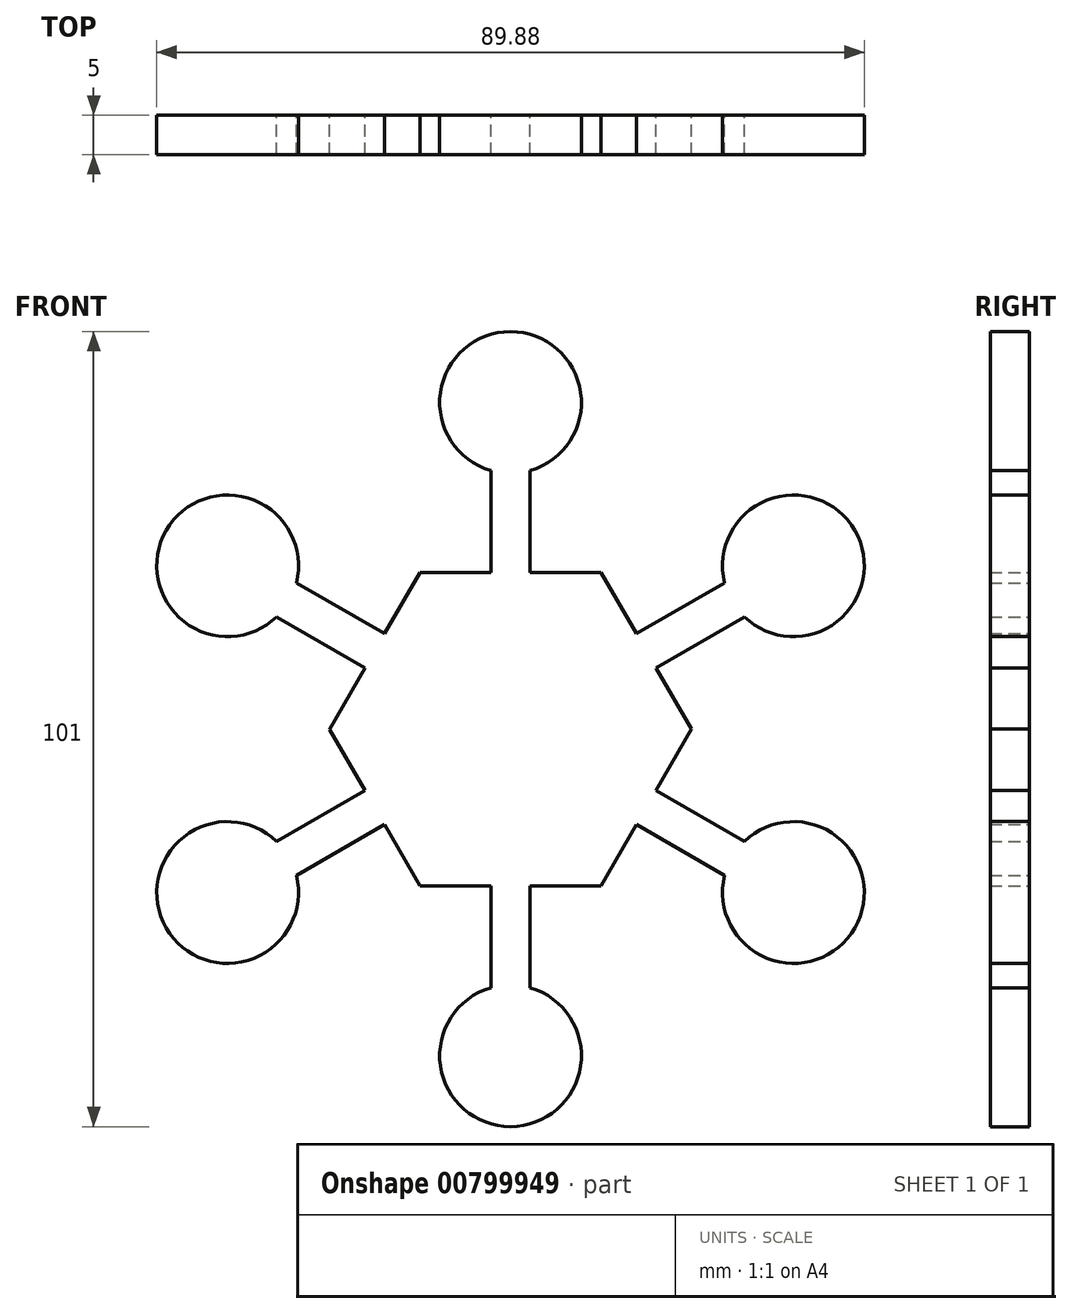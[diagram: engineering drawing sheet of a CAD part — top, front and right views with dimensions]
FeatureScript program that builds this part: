
annotation { "Feature Type Name" : "Feature", "Feature Type Description" : "" }
export const myFeature = defineFeature(function(context is Context, id is Id, definition is map)
    precondition{}
    {
        {
            var Q0;
            Q0=qCreatedBy(makeId("Front.planeOp"),FACE);
            var sketch = newSketch(context, id + "F0", { "sketchPlane" : qUnion([Q0])});
            skLineSegment(sketch, "E0.0", {"start": v(11.49, 19.92) * mm, "end": v(16, 12.12) * mm});
            skLineSegment(sketch, "E0.1", {"start": v(23, 0.01) * mm, "end": v(18.5, -7.8) * mm});
            skLineSegment(sketch, "E0.2", {"start": v(11.51, -19.91) * mm, "end": v(2.5, -19.92) * mm});
            skLineSegment(sketch, "E0.3", {"start": v(-11.49, -19.92) * mm, "end": v(-16, -12.12) * mm});
            skLineSegment(sketch, "E0.4", {"start": v(-23, -0.01) * mm, "end": v(-18.5, 7.8) * mm});
            skLineSegment(sketch, "E0.5", {"start": v(-11.51, 19.91) * mm, "end": v(-2.5, 19.92) * mm});
            skPoint(sketch, "E0.0.midPoint", {"position": v(17.24, 9.97) * mm});
            skLineSegment(sketch, "E1.top", {"start": v(-2.5, 0) * mm, "end": v(2.5, 0) * mm});
            skLineSegment(sketch, "E1.left", {"start": v(-2.5, 32.85) * mm, "end": v(-2.5, 19.76) * mm});
            skLineSegment(sketch, "E1.right", {"start": v(2.5, 32.85) * mm, "end": v(2.5, 19.76) * mm});
            skLineSegment(sketch, "E2.trimOffspring", {"start": v(2.5, 19.92) * mm, "end": v(11.49, 19.92) * mm});
            skArc(sketch, "E3.2.0", {"start": v(2.5, 32.85) * mm, "mid": v(0, 50.5) * mm, "end": v(-2.5, 32.85) * mm});
            skArc(sketch, "E4.1.0", {"start": v(-27.2, 18.6) * mm, "mid": v(-43.73, 25.25) * mm, "end": v(-29.7, 14.26) * mm});
            skArc(sketch, "E4.2.0", {"start": v(-29.7, -14.26) * mm, "mid": v(-43.73, -25.25) * mm, "end": v(-27.2, -18.6) * mm});
            skArc(sketch, "E4.3.0", {"start": v(-2.5, -32.85) * mm, "mid": v(0, -50.5) * mm, "end": v(2.5, -32.85) * mm});
            skArc(sketch, "E4.4.0", {"start": v(27.2, -18.6) * mm, "mid": v(43.73, -25.25) * mm, "end": v(29.7, -14.26) * mm});
            skArc(sketch, "E4.5.0", {"start": v(29.7, 14.26) * mm, "mid": v(43.73, 25.25) * mm, "end": v(27.2, 18.6) * mm});
            skPoint(sketch, "E4.center", {"position": v(0, 0) * mm});
            skLineSegment(sketch, "E5.1.0", {"start": v(-27.2, 18.6) * mm, "end": v(-15.86, 12.05) * mm});
            skLineSegment(sketch, "E5.1.1", {"start": v(-29.7, 14.26) * mm, "end": v(-18.36, 7.72) * mm});
            skLineSegment(sketch, "E5.2.0", {"start": v(-29.7, -14.26) * mm, "end": v(-18.36, -7.72) * mm});
            skLineSegment(sketch, "E5.2.1", {"start": v(-27.2, -18.6) * mm, "end": v(-15.86, -12.05) * mm});
            skLineSegment(sketch, "E5.3.0", {"start": v(-2.5, -32.85) * mm, "end": v(-2.5, -19.76) * mm});
            skLineSegment(sketch, "E5.3.1", {"start": v(2.5, -32.85) * mm, "end": v(2.5, -19.76) * mm});
            skLineSegment(sketch, "E5.4.0", {"start": v(27.2, -18.6) * mm, "end": v(15.86, -12.05) * mm});
            skLineSegment(sketch, "E5.4.1", {"start": v(29.7, -14.26) * mm, "end": v(18.36, -7.72) * mm});
            skLineSegment(sketch, "E5.5.0", {"start": v(29.7, 14.26) * mm, "end": v(18.36, 7.72) * mm});
            skLineSegment(sketch, "E5.5.1", {"start": v(27.2, 18.6) * mm, "end": v(15.86, 12.05) * mm});
            skLineSegment(sketch, "E6.trimOffspring", {"start": v(-16, 12.13) * mm, "end": v(-11.51, 19.91) * mm});
            skLineSegment(sketch, "E7.trimOffspring", {"start": v(-18.5, -7.8) * mm, "end": v(-23, -0.01) * mm});
            skLineSegment(sketch, "E8.trimOffspring", {"start": v(-2.5, -19.92) * mm, "end": v(-11.49, -19.92) * mm});
            skLineSegment(sketch, "E9.trimOffspring", {"start": v(16, -12.13) * mm, "end": v(11.51, -19.91) * mm});
            skLineSegment(sketch, "E10.trimOffspring", {"start": v(18.5, 7.8) * mm, "end": v(23, 0.01) * mm});
            skSolve(sketch);
        }
        {
            var Q0;
            {var subQ20=sQuery(id+"F0.wireOp",EDGE,"E0.0");Q0=makeQuery(id+"F0.imprint","IMPRINT",FACE,{"disambiguationData":[TD([[makeQuery(id+"F0.imprint","IMPRINT",EDGE,{"derivedFrom":subQ20}),-1.0]])]});}
            extrude(context, id + "F1", {"entities" : qUnion([Q0]), "endBound" : BoundingType.SYMMETRIC, "depth" : 5 * mm, "offsetDistance" : 25 * mm});
        }
    });
